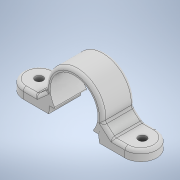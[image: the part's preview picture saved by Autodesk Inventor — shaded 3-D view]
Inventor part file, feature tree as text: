
AUTODESK INVENTOR PART (.ipt)
format: ipt  version: 2022.1 (Build 261234020, 234B)  size: 265,216 bytes
history: native  units: in
note: dims shown in document units (in); Inventor stores cm internally (conversion verified against a paired STEP export)
features: fillet x6, extrude x4, sketch x4
ambient origin geometry x8: Origin, YZ Plane, XZ Plane, XY Plane, X Axis, Y Axis, Z Axis, Center Point
bodies: Solid1 (feature_tree)
feature tree (14):
  extrude  "Extrusion1"  Depth=0.8in
  extrude  "Extrusion2"  Depth=0.8in
  extrude  "Extrusion3"  Depth=1.0in TaperAngle=0.0deg
  extrude  "Extrusion4"  Depth=0.025in TaperAngle=0.0deg
  fillet  "Fillet1"  Radius=0.25in
  fillet  "Fillet2"  Radius=0.25in
  fillet  "Fillet3"  Radius=0.5in
  fillet  "Fillet4"  Radius=0.5in
  fillet  "Fillet5"  Radius=0.5in
  fillet  "Fillet6"  Radius=0.5in
  sketch  "Sketch1"  dims[d0=1.5in d1=0.8in]
  sketch  "Sketch2"  dims[d2=0.8in d3=0.8in]
  sketch  "Sketch3"  dims[d4=0.8in d5=1.0in d6=0.0in]
  sketch  "Sketch4"  dims[d7=0.5in d8=0.0in d9=0.5in d10=0.0in d11=0.25in d12=0.25in d13=0.5in d14=0.5in d15=0.5in d16=0.0in d17=0.5in d18=0.1in d19=0.1in d20=0.1in d21=0.1in d22=0.025in]
